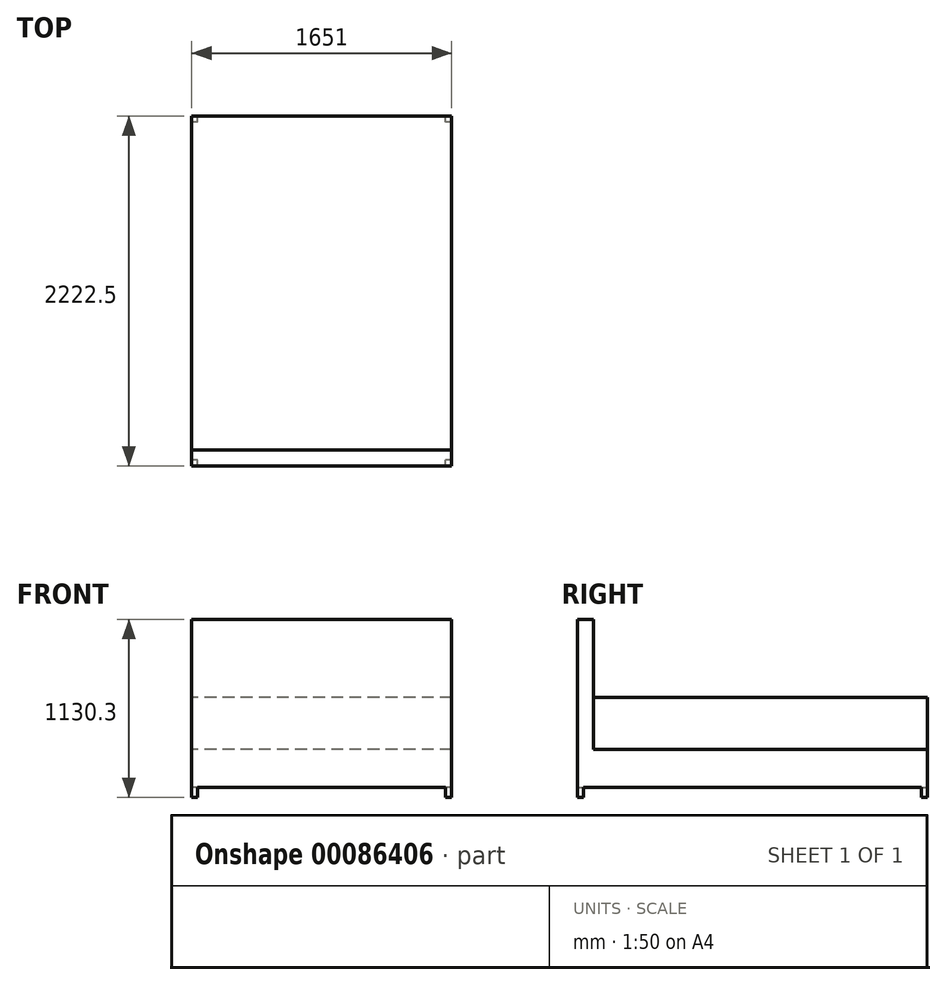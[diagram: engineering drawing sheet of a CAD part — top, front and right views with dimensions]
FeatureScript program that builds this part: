
annotation { "Feature Type Name" : "Feature", "Feature Type Description" : "" }
export const myFeature = defineFeature(function(context is Context, id is Id, definition is map)
    precondition{}
    {
        {
            var Q0;
            Q0=qCreatedBy(makeId("Right.planeOp"),FACE);
            var sketch = newSketch(context, id + "F0", { "sketchPlane" : qUnion([Q0])});
            skLineSegment(sketch, "E0", {"start": v(0, 0) * mm, "end": v(0, 304.8) * mm});
            skLineSegment(sketch, "E1", {"start": v(0, 304.8) * mm, "end": v(-2120.9, 304.8) * mm});
            skLineSegment(sketch, "E2", {"start": v(-2120.9, 304.8) * mm, "end": v(-2120.9, 1130.3) * mm});
            skLineSegment(sketch, "E3", {"start": v(-2120.9, 1130.3) * mm, "end": v(-2222.5, 1130.3) * mm});
            skLineSegment(sketch, "E4", {"start": v(-2222.5, 1130.3) * mm, "end": v(-2222.5, 0) * mm});
            skLineSegment(sketch, "E5", {"start": v(-2222.5, 0) * mm, "end": v(-2184.4, 0) * mm});
            skLineSegment(sketch, "E6", {"start": v(-2184.4, 0) * mm, "end": v(-2184.4, 63.5) * mm});
            skLineSegment(sketch, "E7", {"start": v(-2184.4, 63.5) * mm, "end": v(-38.1, 63.5) * mm});
            skLineSegment(sketch, "E8", {"start": v(-38.1, 63.5) * mm, "end": v(-38.1, 0) * mm});
            skLineSegment(sketch, "E9.trimOffspring", {"start": v(-38.1, 0) * mm, "end": v(0, 0) * mm});
            skSolve(sketch);
        }
        {
            var Q0;
            Q0 = qSketchRegion(id + "F0", true);
            extrude(context, id + "F1", {"entities" : qUnion([Q0]), "endBound" : BoundingType.SYMMETRIC, "depth" : 1651 * mm});
        }
        {
            var Q0;
            Q0=makeQuery(id+"F1.opExtrude","SWEPT_FACE",FACE,{"disambiguationData":[OSD([sQuery(id+"F0.wireOp",EDGE,"E0")])]});
            var sketch = newSketch(context, id + "F2", { "sketchPlane" : qUnion([Q0])});
            skLineSegment(sketch, "E10.bottom", {"start": v(-787.4, 0) * mm, "end": v(787.4, 0) * mm});
            skLineSegment(sketch, "E10.top", {"start": v(-787.4, 63.5) * mm, "end": v(787.4, 63.5) * mm});
            skLineSegment(sketch, "E10.left", {"start": v(-787.4, 0) * mm, "end": v(-787.4, 63.5) * mm});
            skLineSegment(sketch, "E10.right", {"start": v(787.4, 0) * mm, "end": v(787.4, 63.5) * mm});
            skSolve(sketch);
        }
        {
            var Q0;
            Q0 = qSketchRegion(id + "F2", true);
            extrude(context, id + "F3", {"entities" : qUnion([Q0]), "operationType" : NewBodyOperationType.REMOVE, "endBound" : BoundingType.THROUGH_ALL, "oppositeDirection" : true, "depth" : 25.4 * mm});
        }
        {
            var Q0;
            Q0=makeQuery(id+"F1.opExtrude","SWEPT_FACE",FACE,{"disambiguationData":[OSD([sQuery(id+"F0.wireOp",EDGE,"E1")])]});
            var sketch = newSketch(context, id + "F4", { "sketchPlane" : qUnion([Q0])});
            skLineSegment(sketch, "E11.bottom", {"start": v(825.5, 0) * mm, "end": v(-825.5, 0) * mm});
            skLineSegment(sketch, "E11.top", {"start": v(825.5, -2120.9) * mm, "end": v(-825.5, -2120.9) * mm});
            skLineSegment(sketch, "E11.left", {"start": v(825.5, 0) * mm, "end": v(825.5, -2120.9) * mm});
            skLineSegment(sketch, "E11.right", {"start": v(-825.5, 0) * mm, "end": v(-825.5, -2120.9) * mm});
            skSolve(sketch);
        }
        {
            var Q0;
            Q0 = qSketchRegion(id + "F4", true);
            extrude(context, id + "F5", {"entities" : qUnion([Q0]), "depth" : 330.2 * mm});
        }
    });
